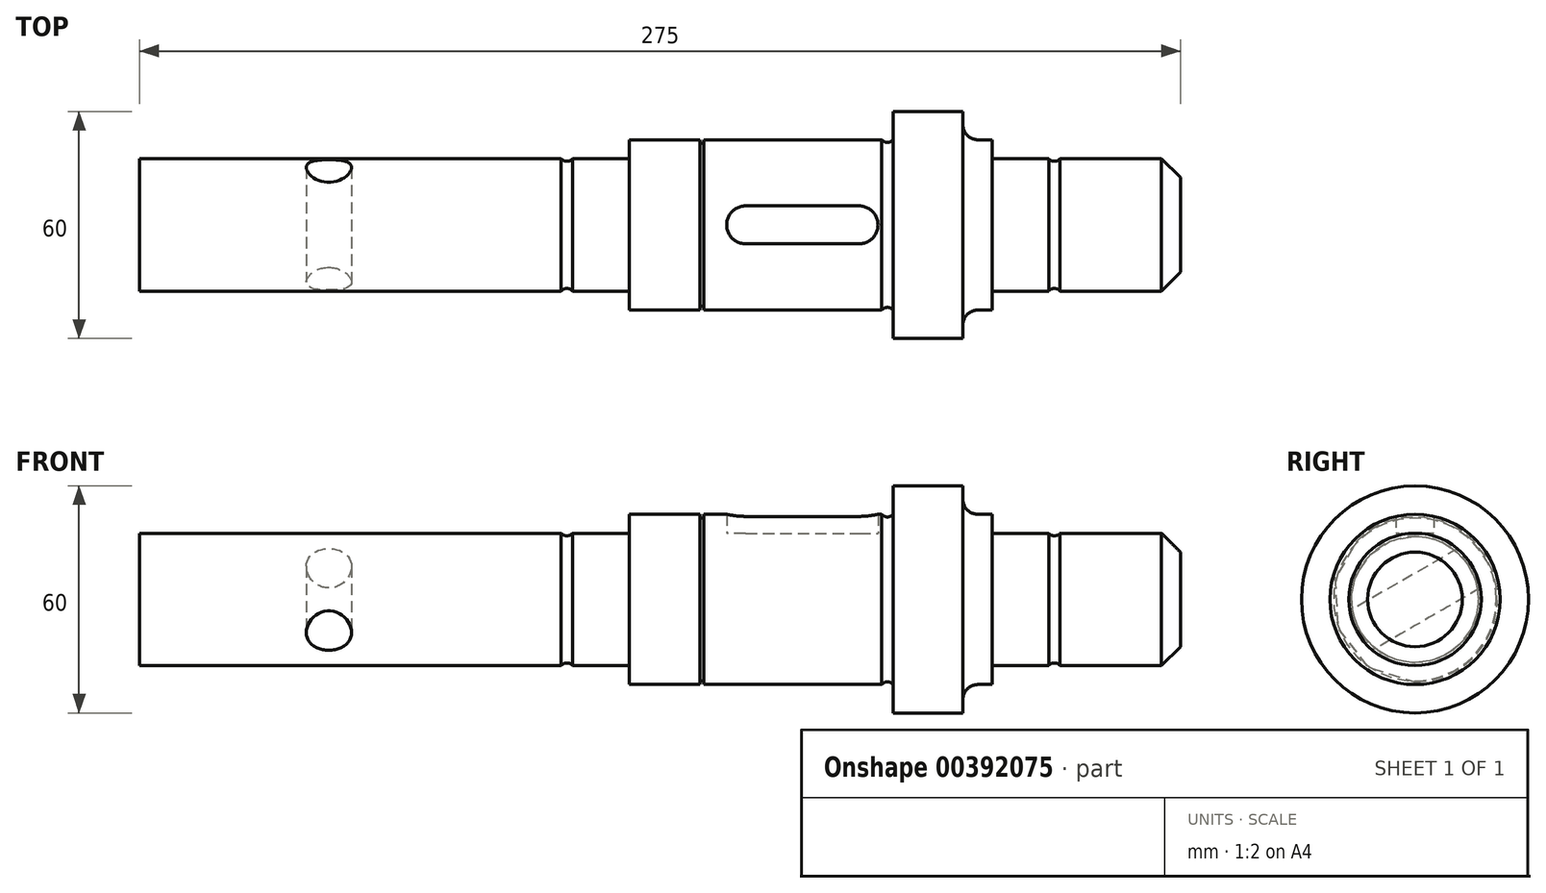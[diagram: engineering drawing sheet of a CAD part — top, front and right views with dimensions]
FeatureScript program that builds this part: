
annotation { "Feature Type Name" : "Feature", "Feature Type Description" : "" }
export const myFeature = defineFeature(function(context is Context, id is Id, definition is map)
    precondition{}
    {
        {
            var Q0;
            Q0=qCreatedBy(makeId("Front.planeOp"),FACE);
            var sketch = newSketch(context, id + "F0", { "sketchPlane" : qUnion([Q0])});
            skLineSegment(sketch, "E0", {"start": v(-207.27, 0) * mm, "end": v(95.62, 0) * mm, "construction": true});
            skLineSegment(sketch, "E1", {"start": v(-199.1, 0) * mm, "end": v(-199.1, 17.5) * mm});
            skLineSegment(sketch, "E2", {"start": v(-199.1, 17.5) * mm, "end": v(-69.7, 17.5) * mm});
            skLineSegment(sketch, "E3", {"start": v(-69.7, 17.5) * mm, "end": v(-69.7, 22.5) * mm});
            skLineSegment(sketch, "E4", {"start": v(-69.7, 22.5) * mm, "end": v(0, 22.5) * mm});
            skLineSegment(sketch, "E5", {"start": v(0, 22.5) * mm, "end": v(0, 30) * mm});
            skLineSegment(sketch, "E6", {"start": v(0, 30) * mm, "end": v(18.4, 30) * mm});
            skLineSegment(sketch, "E7", {"start": v(18.4, 30) * mm, "end": v(18.4, 26.5) * mm});
            skLineSegment(sketch, "E8", {"start": v(22.4, 22.5) * mm, "end": v(26.1, 22.5) * mm});
            skLineSegment(sketch, "E9", {"start": v(26.1, 22.5) * mm, "end": v(26.1, 17.5) * mm});
            skLineSegment(sketch, "E10", {"start": v(26.1, 17.5) * mm, "end": v(70.9, 17.5) * mm});
            skLineSegment(sketch, "E11", {"start": v(75.9, 12.5) * mm, "end": v(75.9, 0) * mm});
            skLineSegment(sketch, "E12", {"start": v(-199.1, 0) * mm, "end": v(75.9, 0) * mm});
            skLineSegment(sketch, "E13", {"start": v(70.9, 17.5) * mm, "end": v(75.9, 12.5) * mm});
            skPoint(sketch, "E14.visualSharp", {"position": v(18.4, 22.5) * mm});
            skArc(sketch, "E14.filletArc", {"start": v(18.4, 26.5) * mm, "mid": v(19.57, 23.67) * mm, "end": v(22.4, 22.5) * mm});
            skSolve(sketch);
        }
        {
            var Q0;
            Q0 = qSketchRegion(id + "F0", true);
            var Q1;
            Q1=sQuery(id+"F0.wireOp",EDGE,"E0");
            revolve(context, id + "F1", {"entities" : qUnion([Q0]), "axis" : qUnion([Q1]), "revolveType" : RevolveType.FULL});
        }
        {
            var Q0;
            Q0=qCreatedBy(makeId("Front.planeOp"),FACE);
            var sketch = newSketch(context, id + "F2", { "sketchPlane" : qUnion([Q0])});
            skLineSegment(sketch, "E15.bottom", {"start": v(-51, 33.5) * mm, "end": v(-50, 33.5) * mm});
            skLineSegment(sketch, "E15.top", {"start": v(-51, 21.5) * mm, "end": v(-50, 21.5) * mm});
            skLineSegment(sketch, "E15.left", {"start": v(-51, 33.5) * mm, "end": v(-51, 21.5) * mm});
            skLineSegment(sketch, "E15.right", {"start": v(-50, 33.5) * mm, "end": v(-50, 21.5) * mm});
            skSolve(sketch);
        }
        {
            var Q0;
            Q0 = qSketchRegion(id + "F2", true);
            var Q1;
            Q1=sQuery(id+"F0.wireOp",EDGE,"E0");
            revolve(context, id + "F3", {"operationType" : NewBodyOperationType.REMOVE, "entities" : qUnion([Q0]), "axis" : qUnion([Q1]), "revolveType" : RevolveType.FULL, "oppositeDirection" : true});
        }
        {
            var Q0;
            Q0=qCreatedBy(makeId("Front.planeOp"),FACE);
            var sketch = newSketch(context, id + "F4", { "sketchPlane" : qUnion([Q0])});
            skCircle(sketch, "E16", {"center": v(-86.2, 18.76) * mm, "radius": 1.96 * mm});
            skPoint(sketch, "E17", {"position": v(-84.7, 17.5) * mm});
            skPoint(sketch, "E18", {"position": v(-87.7, 17.5) * mm});
            skCircle(sketch, "E19", {"center": v(42.6, 18.76) * mm, "radius": 1.96 * mm});
            skPoint(sketch, "E20", {"position": v(44.1, 17.5) * mm});
            skPoint(sketch, "E21", {"position": v(41.1, 17.5) * mm});
            skArc(sketch, "E22", {"start": v(-3.46, 23.76) * mm, "mid": v(-2.17, 21.92) * mm, "end": v(0, 22.5) * mm});
            skPoint(sketch, "E23", {"position": v(0, 22.5) * mm});
            skPoint(sketch, "E24", {"position": v(-3, 22.5) * mm});
            skLineSegment(sketch, "E25", {"start": v(-3.46, 23.76) * mm, "end": v(-3.46, 32.4) * mm});
            skLineSegment(sketch, "E26", {"start": v(-3.46, 32.4) * mm, "end": v(0, 32.4) * mm});
            skLineSegment(sketch, "E27", {"start": v(0, 32.4) * mm, "end": v(0, 22.5) * mm});
            skSolve(sketch);
        }
        {
            var Q0;
            Q0 = qSketchRegion(id + "F4", true);
            var Q1;
            Q1=sQuery(id+"F0.wireOp",EDGE,"E0");
            revolve(context, id + "F5", {"operationType" : NewBodyOperationType.REMOVE, "entities" : qUnion([Q0]), "axis" : qUnion([Q1]), "revolveType" : RevolveType.FULL, "oppositeDirection" : true});
        }
        {
            var Q0;
            Q0=qCreatedBy(makeId("Top.planeOp"),FACE);
            var sketch = newSketch(context, id + "F6", { "sketchPlane" : qUnion([Q0])});
            skArc(sketch, "E28", {"start": v(-39, 5) * mm, "mid": v(-44, 0) * mm, "end": v(-39, -5) * mm});
            skArc(sketch, "E29", {"start": v(-9, -5) * mm, "mid": v(-4, 0) * mm, "end": v(-9, 5) * mm});
            skLineSegment(sketch, "E30", {"start": v(-39, 5) * mm, "end": v(-9, 5) * mm});
            skLineSegment(sketch, "E31", {"start": v(-39, -5) * mm, "end": v(-9, -5) * mm});
            skSolve(sketch);
        }
        {
            var Q0;
            Q0 = qSketchRegion(id + "F6", true);
            extrude(context, id + "F7", {"entities" : qUnion([Q0]), "operationType" : NewBodyOperationType.REMOVE, "depth" : 60 * mm, "hasSecondDirection" : true, "secondDirectionOppositeDirection" : false, "secondDirectionDepth" : (45 / 2 - 5) * mm});
        }
        {
            var Q0;
            Q0=qCreatedBy(makeId("Right.planeOp"),FACE);
            cPlane(context, id + "F8", {"entities" : qUnion([Q0]), "cplaneType" : CPlaneType.OFFSET, "offset" : (69.7 + 79.4) * mm, "oppositeDirection" : true, "width" : 150 * mm, "height" : 150 * mm});
        }
        {
            var Q0;
            Q0=qCreatedBy(id+"F8.planeOp",FACE);
            var sketch = newSketch(context, id + "F9", { "sketchPlane" : qUnion([Q0])});
            skLineSegment(sketch, "E32", {"start": v(30.77, 17.76) * mm, "end": v(-51.15, -29.53) * mm, "construction": true});
            skPoint(sketch, "E33", {"position": v(0, 0) * mm});
            skSolve(sketch);
        }
        {
            var Q0;
            Q0=sQuery(id+"F9.wireOp",VERTEX,"E33");
            var Q1;
            Q1=sQuery(id+"F9.wireOp",EDGE,"E32");
            cPlane(context, id + "F10", {"entities" : qUnion([Q0, Q1]), "cplaneType" : CPlaneType.LINE_POINT, "offset" : 25 * mm, "width" : 150 * mm, "height" : 150 * mm});
        }
        {
            var Q0;
            Q0=qCreatedBy(id+"F10.planeOp",FACE);
            var sketch = newSketch(context, id + "F11", { "sketchPlane" : qUnion([Q0])});
            skCircle(sketch, "E34", {"center": v(-149.1, 0) * mm, "radius": 6 * mm});
            skSolve(sketch);
        }
        {
            var Q0;
            Q0 = qSketchRegion(id + "F11", true);
            extrude(context, id + "F12", {"entities" : qUnion([Q0]), "operationType" : NewBodyOperationType.REMOVE, "oppositeDirection" : true, "depth" : 25 * mm, "hasSecondDirection" : true, "secondDirectionOppositeDirection" : false, "secondDirectionDepth" : 25 * mm});
        }
    });
